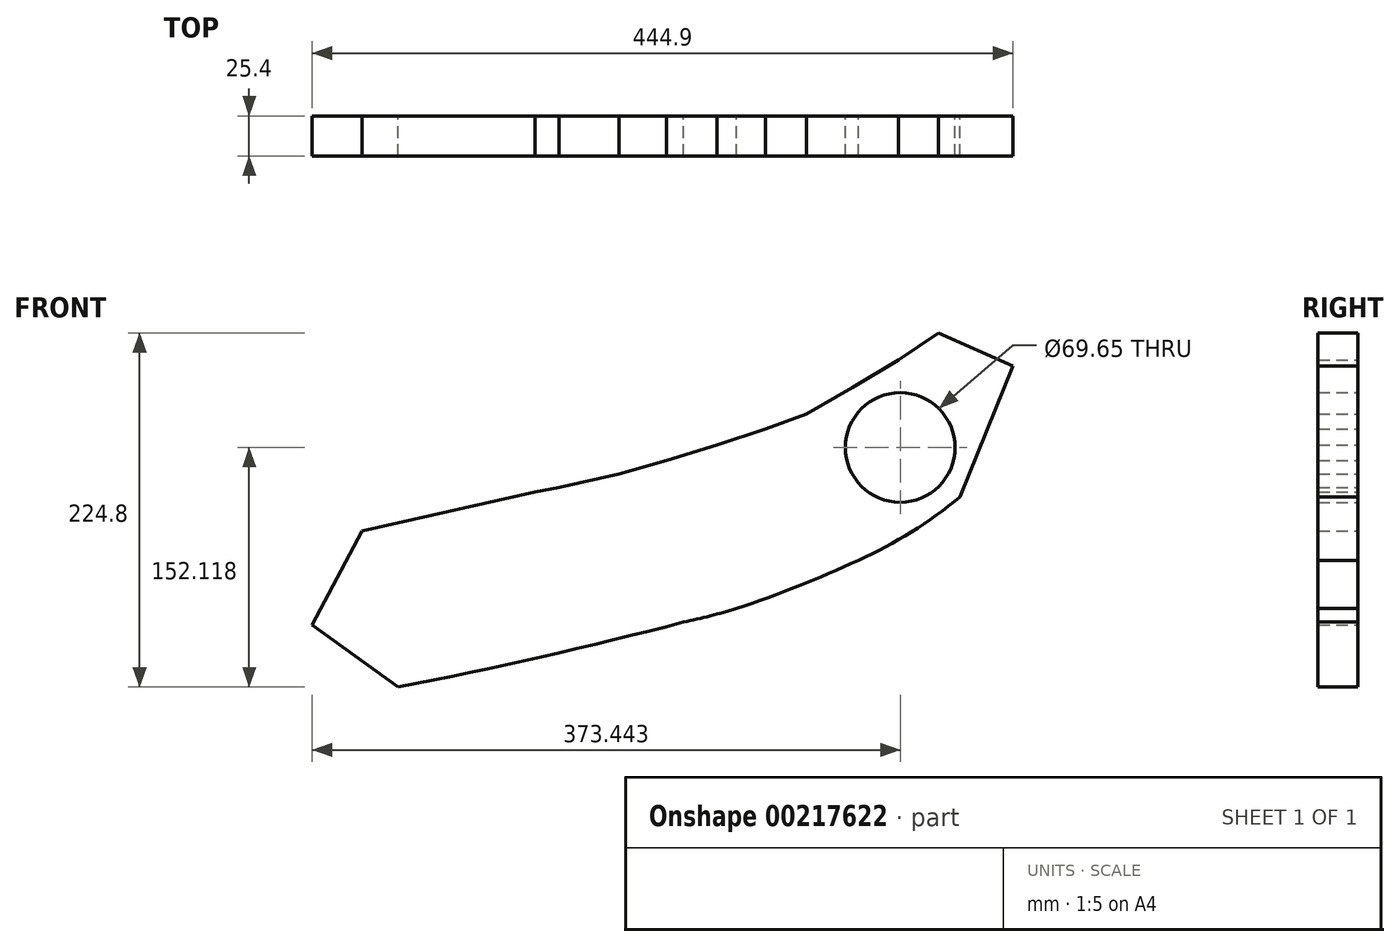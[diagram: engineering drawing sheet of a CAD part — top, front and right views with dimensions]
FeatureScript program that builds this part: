
annotation { "Feature Type Name" : "Feature", "Feature Type Description" : "" }
export const myFeature = defineFeature(function(context is Context, id is Id, definition is map)
    precondition{}
    {
        {
            var Q0;
            Q0=qCreatedBy(makeId("Front.planeOp"),FACE);
            var sketch = newSketch(context, id + "F0", { "sketchPlane" : qUnion([Q0])});
            skLineSegment(sketch, "E0", {"start": v(45.75, -55.23) * mm, "end": v(79.2, 27.8) * mm});
            skArc(sketch, "E1", {"start": v(-18.7, -95.52) * mm, "mid": v(14.9, -77.57) * mm, "end": v(45.75, -55.23) * mm});
            skArc(sketch, "E2", {"start": v(-96.16, -126.28) * mm, "mid": v(-56.99, -112.02) * mm, "end": v(-18.7, -95.52) * mm});
            skArc(sketch, "E3", {"start": v(-129.85, -134.85) * mm, "mid": v(-112.93, -130.88) * mm, "end": v(-96.16, -126.28) * mm});
            skArc(sketch, "E4", {"start": v(-312.01, -176.2) * mm, "mid": v(-220.6, -157.01) * mm, "end": v(-129.85, -134.85) * mm});
            skLineSegment(sketch, "E5", {"start": v(-311.17, -176.03) * mm, "end": v(-365.7, -136.64) * mm});
            skLineSegment(sketch, "E6", {"start": v(-334.07, -76.84) * mm, "end": v(-365.7, -136.64) * mm});
            skLineSegment(sketch, "E7", {"start": v(-334.07, -76.84) * mm, "end": v(-224.2, -52.17) * mm});
            skLineSegment(sketch, "E8", {"start": v(79.2, 27.8) * mm, "end": v(32.06, 48.77) * mm});
            skPoint(sketch, "E9.orphan", {"position": v(26.6, 51.2) * mm});
            skPoint(sketch, "E10.orphan", {"position": v(35.3, 51.2) * mm});
            skCircle(sketch, "E11", {"center": v(7.73, -23.91) * mm, "radius": 34.83 * mm});
            skLineSegment(sketch, "E12", {"start": v(32.06, 48.77) * mm, "end": v(6.72, 31.56) * mm});
            skLineSegment(sketch, "E13", {"start": v(6.72, 31.56) * mm, "end": v(-22.75, 14.25) * mm});
            skLineSegment(sketch, "E14", {"start": v(-22.75, 14.25) * mm, "end": v(-51.72, -2.54) * mm});
            skLineSegment(sketch, "E15", {"start": v(-51.72, -2.54) * mm, "end": v(-77.93, -12.3) * mm});
            skLineSegment(sketch, "E16", {"start": v(-77.93, -12.3) * mm, "end": v(-108.78, -22.42) * mm});
            skLineSegment(sketch, "E17", {"start": v(-108.78, -22.42) * mm, "end": v(-140.82, -32.02) * mm});
            skLineSegment(sketch, "E18", {"start": v(-140.82, -32.02) * mm, "end": v(-170.98, -40.58) * mm});
            skLineSegment(sketch, "E19", {"start": v(-170.98, -40.58) * mm, "end": v(-208.86, -49.32) * mm});
            skLineSegment(sketch, "E20", {"start": v(-208.86, -49.32) * mm, "end": v(-224.2, -52.17) * mm});
            skSolve(sketch);
        }
        {
            var Q0;
            Q0 = qSketchRegion(id + "F0", true);
            extrude(context, id + "F1", {"entities" : qUnion([Q0]), "depth" : 3.17 * mm});
        }
        {
            var Q0;
            Q0 = qSketchRegion(id + "F0", true);
            extrude(context, id + "F2", {"entities" : qUnion([Q0]), "operationType" : NewBodyOperationType.ADD, "depth" : 25.4 * mm});
        }
    });
